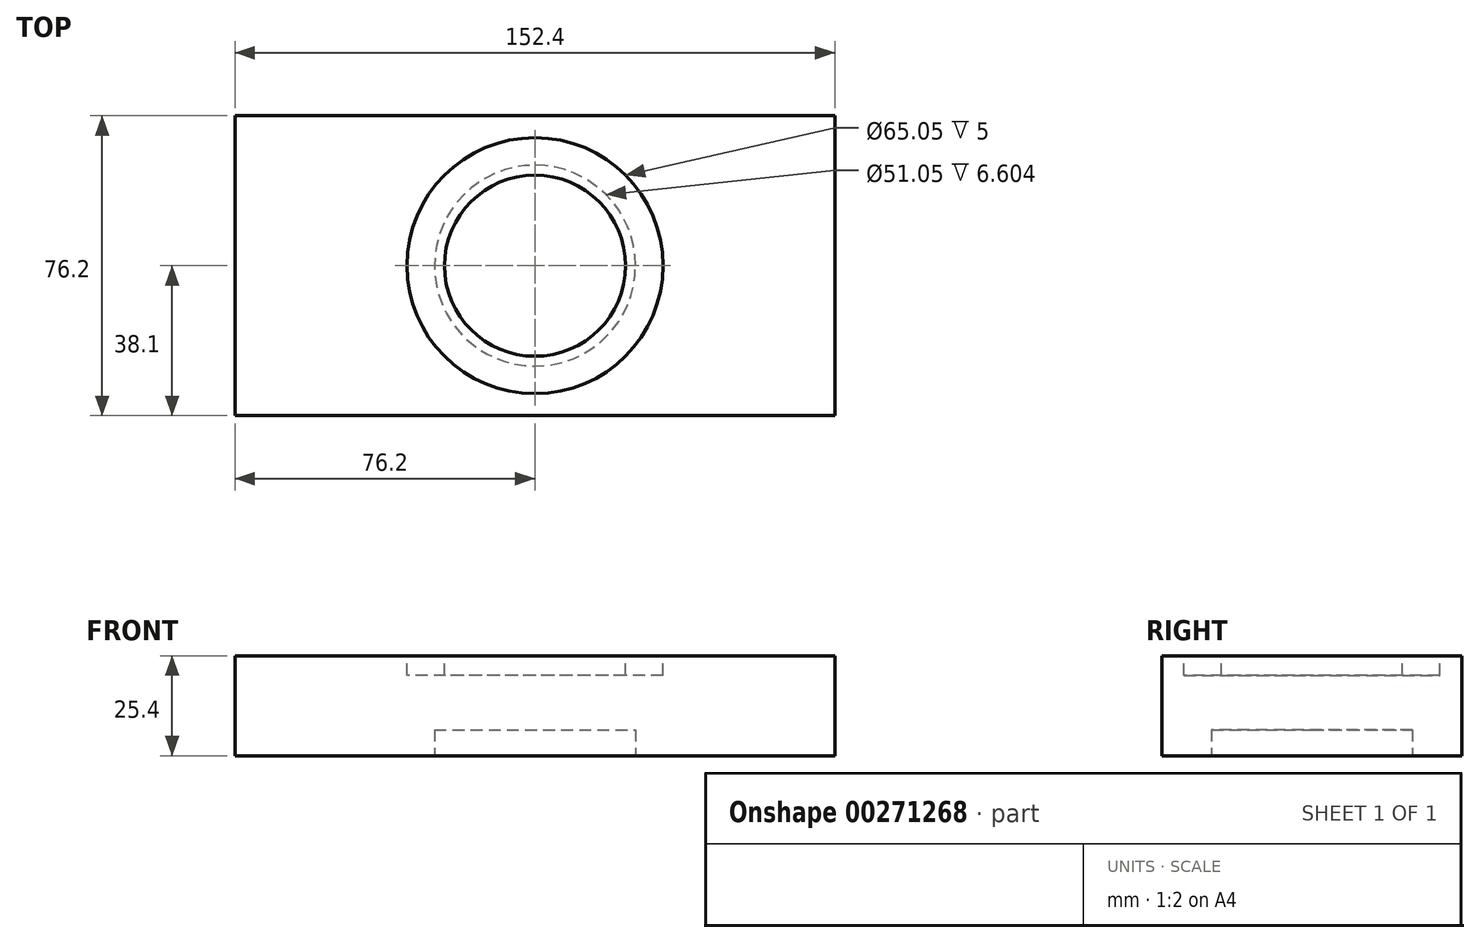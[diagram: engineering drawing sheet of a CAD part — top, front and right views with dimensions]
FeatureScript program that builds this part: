
annotation { "Feature Type Name" : "Feature", "Feature Type Description" : "" }
export const myFeature = defineFeature(function(context is Context, id is Id, definition is map)
    precondition{}
    {
        {
            var Q0;
            Q0=qCreatedBy(makeId("Top.planeOp"),FACE);
            var sketch = newSketch(context, id + "F0", { "sketchPlane" : qUnion([Q0])});
            skLineSegment(sketch, "E0.bottom", {"start": v(-76.2, 38.1) * mm, "end": v(76.2, 38.1) * mm});
            skLineSegment(sketch, "E0.top", {"start": v(-76.2, -38.1) * mm, "end": v(76.2, -38.1) * mm});
            skLineSegment(sketch, "E0.left", {"start": v(-76.2, 38.1) * mm, "end": v(-76.2, -38.1) * mm});
            skLineSegment(sketch, "E0.right", {"start": v(76.2, 38.1) * mm, "end": v(76.2, -38.1) * mm});
            skCircle(sketch, "E1", {"center": v(0, 0) * mm, "radius": 23.5 * mm});
            skCircle(sketch, "E2", {"center": v(0, 0) * mm, "radius": 23 * mm});
            skCircle(sketch, "E3", {"center": v(0, 0) * mm, "radius": 32.52 * mm});
            skSolve(sketch);
        }
        {
            var Q0;
            Q0=makeQuery(id+"F0.imprint","IMPRINT",FACE,{"disambiguationData":[TD([[makeQuery(id+"F0.imprint","IMPRINT",EDGE,{"derivedFrom":sQuery(id+"F0.wireOp",EDGE,"E0.bottom")}),-1.0]])]});
            var Q1;
            Q1=makeQuery(id+"F0.imprint","IMPRINT",FACE,{"disambiguationData":[TD([[makeQuery(id+"F0.imprint","IMPRINT",EDGE,{"derivedFrom":sQuery(id+"F0.wireOp",EDGE,"E1")}),-1.0]])]});
            var Q2;
            Q2=makeQuery(id+"F0.imprint","IMPRINT",FACE,{"disambiguationData":[TD([[makeQuery(id+"F0.imprint","IMPRINT",EDGE,{"derivedFrom":sQuery(id+"F0.wireOp",EDGE,"E2")}),1.0]])]});
            var Q3;
            Q3=makeQuery(id+"F0.imprint","IMPRINT",FACE,{"disambiguationData":[TD([[makeQuery(id+"F0.imprint","IMPRINT",EDGE,{"derivedFrom":sQuery(id+"F0.wireOp",EDGE,"E1")}),1.0]])]});
            extrude(context, id + "F1", {"entities" : qUnion([Q0, Q1, Q2, Q3]), "oppositeDirection" : true, "depth" : 25.4 * mm});
        }
        {
            var Q0;
            Q0=makeQuery(id+"F0.imprint","IMPRINT",FACE,{"disambiguationData":[TD([[makeQuery(id+"F0.imprint","IMPRINT",EDGE,{"derivedFrom":sQuery(id+"F0.wireOp",EDGE,"E1")}),-1.0]])]});
            var Q1;
            Q1=makeQuery(id+"F0.imprint","IMPRINT",FACE,{"disambiguationData":[TD([[makeQuery(id+"F0.imprint","IMPRINT",EDGE,{"derivedFrom":sQuery(id+"F0.wireOp",EDGE,"E1")}),1.0]])]});
            extrude(context, id + "F2", {"entities" : qUnion([Q0, Q1]), "operationType" : NewBodyOperationType.REMOVE, "oppositeDirection" : true, "depth" : 5 * mm});
        }
        {
            var Q0;
            Q0=makeQuery(id+"F1.opExtrude","CAP_FACE",FACE,{"disambiguationData":[OSD([sQuery(id+"F0.wireOp",EDGE,"E0.bottom"),sQuery(id+"F0.wireOp",EDGE,"E0.top"),sQuery(id+"F0.wireOp",EDGE,"E0.left"),sQuery(id+"F0.wireOp",EDGE,"E0.right")])],"isStart":false});
            var sketch = newSketch(context, id + "F3", { "sketchPlane" : qUnion([Q0])});
            skCircle(sketch, "E4", {"center": v(0, 0) * mm, "radius": 25.53 * mm});
            skSolve(sketch);
        }
        {
            var Q0;
            Q0 = qSketchRegion(id + "F3", true);
            extrude(context, id + "F4", {"entities" : qUnion([Q0]), "operationType" : NewBodyOperationType.REMOVE, "oppositeDirection" : true, "depth" : 6.6 * mm});
        }
    });
